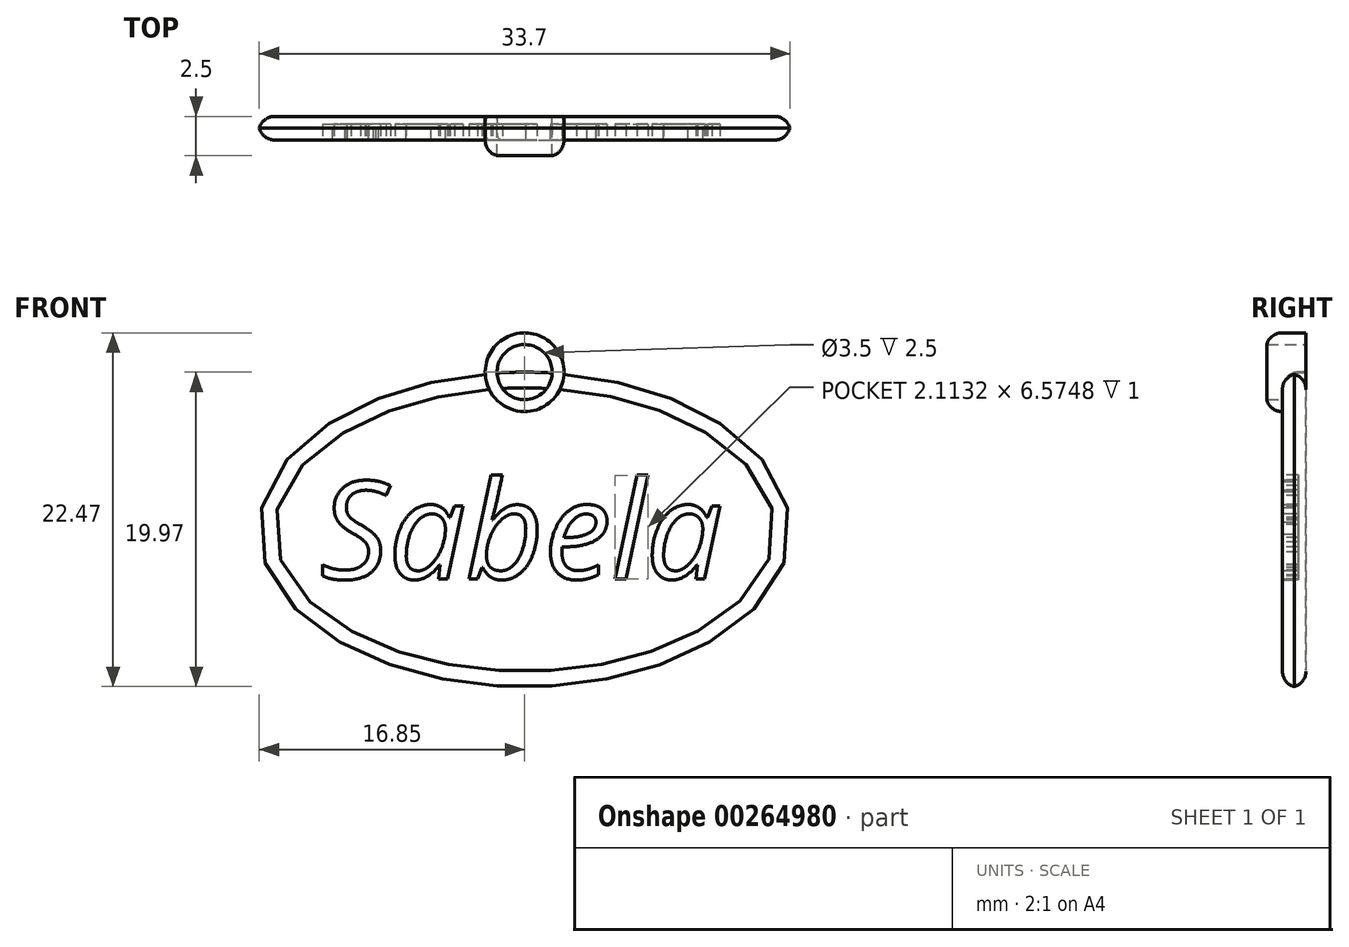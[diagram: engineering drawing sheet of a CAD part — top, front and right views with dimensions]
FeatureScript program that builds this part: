
annotation { "Feature Type Name" : "Feature", "Feature Type Description" : "" }
export const myFeature = defineFeature(function(context is Context, id is Id, definition is map)
    precondition{}
    {
        {
            var Q0;
            Q0=qCreatedBy(makeId("Front.planeOp"),FACE);
            var sketch = newSketch(context, id + "F0", { "sketchPlane" : qUnion([Q0])});
            skEllipse(sketch, "E0", {"center": v(0, 0) * mm, "majorRadius": 16.89 * mm, "minorRadius": 10 * mm, "majorAxis": v(1, 0)});
            skSolve(sketch);
        }
        {
            var Q0;
            Q0 = qSketchRegion(id + "F0", true);
            extrude(context, id + "F1", {"entities" : qUnion([Q0]), "depth" : 1.5 * mm});
        }
        {
            var Q0;
            Q0=qCreatedBy(makeId("Front.planeOp"),FACE);
            var sketch = newSketch(context, id + "F2", { "sketchPlane" : qUnion([Q0])});
            skPoint(sketch, "E1", {"position": v(0, 10.64) * mm});
            skCircle(sketch, "E2", {"center": v(0, 10) * mm, "radius": 2.5 * mm});
            skCircle(sketch, "E3", {"center": v(0, 10) * mm, "radius": 1.75 * mm});
            skSolve(sketch);
        }
        {
            var Q0;
            Q0 = qSketchRegion(id + "F2", true);
            extrude(context, id + "F3", {"entities" : qUnion([Q0]), "operationType" : NewBodyOperationType.ADD, "depth" : 2.5 * mm});
        }
        {
            var Q0;
            Q0=makeQuery(id+"F3.opExtrude","CAP_EDGE",EDGE,{"disambiguationData":[OSD([sQuery(id+"F2.wireOp",EDGE,"E2")])],"isStart":false});
            var Q1;
            {var subQ0=sQuery(id+"F0.wireOp",EDGE,"E0");Q1=makeQuery(id+"F3.boolean.opBoolean","SPLIT",EDGE,{"disambiguationData":[TD([makeQuery(id+"F3.opExtrude","SWEPT_FACE",FACE,{"disambiguationData":[OSD([sQuery(id+"F2.wireOp",EDGE,"E3")])]})])],"derivedFrom":makeQuery(id+"F1.opExtrude","CAP_EDGE",EDGE,{"disambiguationData":[OSD([subQ0])],"isStart":false})});}
            var Q2;
            {var subQ0=sQuery(id+"F0.wireOp",EDGE,"E0");Q2=makeQuery(id+"F3.boolean.opBoolean","SPLIT",EDGE,{"disambiguationData":[TD([makeQuery(id+"F3.opExtrude","SWEPT_FACE",FACE,{"disambiguationData":[OSD([sQuery(id+"F2.wireOp",EDGE,"E2")])]})])],"derivedFrom":makeQuery(id+"F1.opExtrude","CAP_EDGE",EDGE,{"disambiguationData":[OSD([subQ0])],"isStart":false})});}
            var Q3;
            {var subQ0=sQuery(id+"F0.wireOp",EDGE,"E0");var subQ1=sQuery(id+"F2.wireOp",EDGE,"E2");Q3=makeQuery(id+"F3.boolean.opBoolean","SPLIT",EDGE,{"disambiguationData":[TD([makeQuery(id+"F3.opExtrude","SWEPT_FACE",FACE,{"disambiguationData":[OSD([subQ1])]})])],"derivedFrom":makeQuery(id+"F1.opExtrude","CAP_EDGE",EDGE,{"disambiguationData":[OSD([subQ0])],"isStart":true})});}
            fillet(context, id + "F4", {"entities" : qUnion([Q0, Q1, Q2, Q3]), "radius" : 1 * mm, "tangentPropagation" : true, "allowEdgeOverflow" : false});
        }
        {
            var Q0;
            {var subQ0=sQuery(id+"F0.wireOp",EDGE,"E0");Q0=makeQuery(id+"F3.boolean.opBoolean","SPLIT",FACE,{"disambiguationData":[TD([makeQuery(id+"F3.opExtrude","SWEPT_FACE",FACE,{"disambiguationData":[OSD([sQuery(id+"F2.wireOp",EDGE,"E2")])]})])],"derivedFrom":makeQuery(id+"F1.opExtrude","CAP_FACE",FACE,{"disambiguationData":[OSD([subQ0])],"isStart":false})});}
            var sketch = newSketch(context, id + "F5", { "sketchPlane" : qUnion([Q0])});
            skText(sketch, "E4", { "text": "Sabela", "fontName": "OpenSans-Italic.ttf"});
            const initialGuessF5  = {"E4": [-0.013, -0.00312, 1, 0, 0.00623]};
            skSetInitialGuess(sketch, initialGuessF5);
            skSolve(sketch);
        }
        {
            var Q0;
            Q0 = qSketchRegion(id + "F5", true);
            extrude(context, id + "F6", {"entities" : qUnion([Q0]), "operationType" : NewBodyOperationType.REMOVE, "oppositeDirection" : true, "depth" : 1 * mm});
        }
    });
